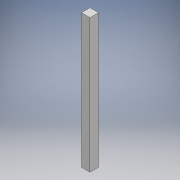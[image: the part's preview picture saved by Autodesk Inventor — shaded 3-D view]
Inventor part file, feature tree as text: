
AUTODESK INVENTOR PART (.ipt)
format: ipt  version: 2017 (Build 210142000, 142)  size: 91,136 bytes
history: native  units: mm
features: extrude x1, sketch x1
ambient origin geometry x8: Origin, YZ Plane, XZ Plane, XY Plane, X Axis, Y Axis, Z Axis, Center Point
bodies: Solid1 (feature_tree)
feature tree (2):
  extrude  "Extrusion1"  Depth=150.0mm TaperAngle=0.0deg
  sketch  "Sketch1"  dims[d0=9.525mm d1=150.0mm d2=0.0mm]
